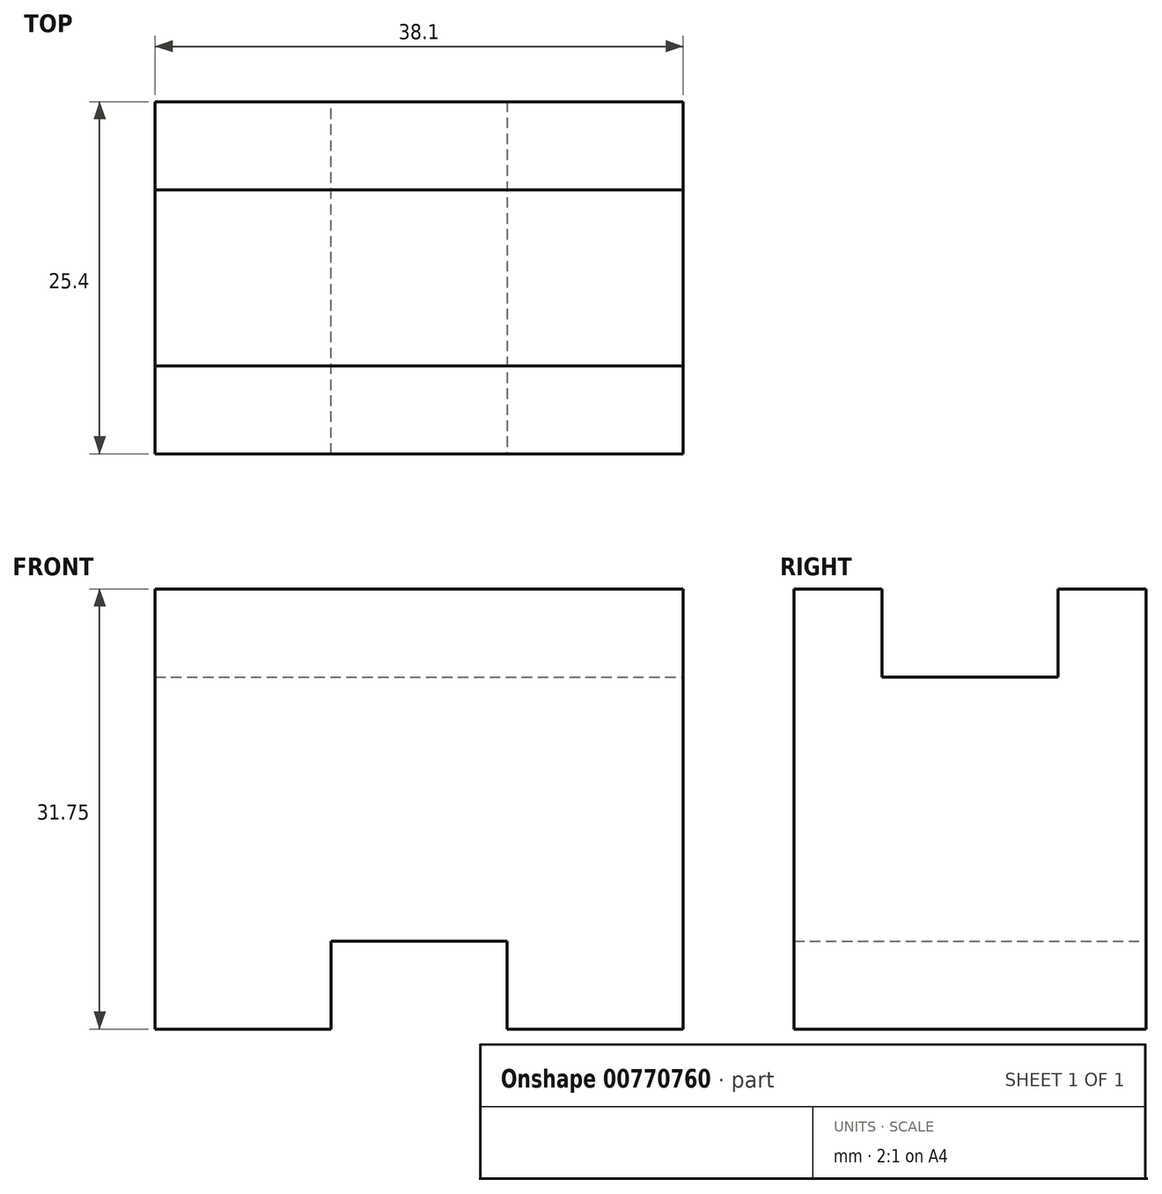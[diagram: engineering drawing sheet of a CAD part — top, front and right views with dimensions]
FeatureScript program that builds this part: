
annotation { "Feature Type Name" : "Feature", "Feature Type Description" : "" }
export const myFeature = defineFeature(function(context is Context, id is Id, definition is map)
    precondition{}
    {
        {
            var Q0;
            Q0=qCreatedBy(makeId("Front.planeOp"),FACE);
            var sketch = newSketch(context, id + "F0", { "sketchPlane" : qUnion([Q0])});
            skLineSegment(sketch, "E0", {"start": v(0, 0) * mm, "end": v(38.1, 0) * mm});
            skLineSegment(sketch, "E1", {"start": v(38.1, 0) * mm, "end": v(38.1, 31.75) * mm});
            skLineSegment(sketch, "E2", {"start": v(38.1, 31.75) * mm, "end": v(0, 31.75) * mm});
            skLineSegment(sketch, "E3", {"start": v(0, 31.75) * mm, "end": v(0, 0) * mm});
            skSolve(sketch);
        }
        {
            var Q0;
            Q0=makeQuery(id+"F0.imprint","IMPRINT",FACE,{"disambiguationData":[TD([[makeQuery(id+"F0.imprint","IMPRINT",EDGE,{"derivedFrom":sQuery(id+"F0.wireOp",EDGE,"E0")}),1.0]])]});
            extrude(context, id + "F1", {"entities" : qUnion([Q0]), "depth" : 25.4 * mm, "offsetDistance" : 25.4 * mm});
        }
        {
            var Q0;
            Q0=makeQuery(id+"F1.opExtrude","SWEPT_FACE",FACE,{"disambiguationData":[OSD([sQuery(id+"F0.wireOp",EDGE,"E2")])]});
            var sketch = newSketch(context, id + "F2", { "sketchPlane" : qUnion([Q0])});
            skLineSegment(sketch, "E4", {"start": v(0, -6.35) * mm, "end": v(38.1, -6.35) * mm});
            skLineSegment(sketch, "E5", {"start": v(38.1, -6.35) * mm, "end": v(38.1, -19.05) * mm});
            skLineSegment(sketch, "E6", {"start": v(38.1, -19.05) * mm, "end": v(0, -19.05) * mm});
            skLineSegment(sketch, "E7", {"start": v(0, -19.05) * mm, "end": v(0, -6.35) * mm});
            skSolve(sketch);
        }
        {
            var Q0;
            Q0=makeQuery(id+"F2.imprint","IMPRINT",FACE,{"disambiguationData":[TD([[makeQuery(id+"F2.imprint","IMPRINT",EDGE,{"derivedFrom":sQuery(id+"F2.wireOp",EDGE,"E4")}),-1.0]])]});
            extrude(context, id + "F3", {"entities" : qUnion([Q0]), "operationType" : NewBodyOperationType.REMOVE, "oppositeDirection" : true, "depth" : 6.35 * mm, "offsetDistance" : 25.4 * mm});
        }
        {
            var Q0;
            Q0=makeQuery(id+"F1.opExtrude","SWEPT_FACE",FACE,{"disambiguationData":[OSD([sQuery(id+"F0.wireOp",EDGE,"E0")])]});
            var sketch = newSketch(context, id + "F4", { "sketchPlane" : qUnion([Q0])});
            skLineSegment(sketch, "E8", {"start": v(12.7, 25.4) * mm, "end": v(12.7, 0) * mm});
            skLineSegment(sketch, "E9", {"start": v(12.7, 0) * mm, "end": v(25.4, 0) * mm});
            skLineSegment(sketch, "E10", {"start": v(25.4, 0) * mm, "end": v(25.4, 25.4) * mm});
            skSolve(sketch);
        }
        {
            var Q0;
            {var subQ0=sQuery(id+"F4.wireOp",EDGE,"E8");Q0=makeQuery(id+"F4.imprint","IMPRINT",FACE,{"disambiguationData":[TD([[makeQuery(id+"F4.imprint","IMPRINT",EDGE,{"derivedFrom":subQ0}),1.0]])]});}
            extrude(context, id + "F5", {"entities" : qUnion([Q0]), "operationType" : NewBodyOperationType.REMOVE, "oppositeDirection" : true, "depth" : 6.35 * mm, "offsetDistance" : 25.4 * mm});
        }
    });
